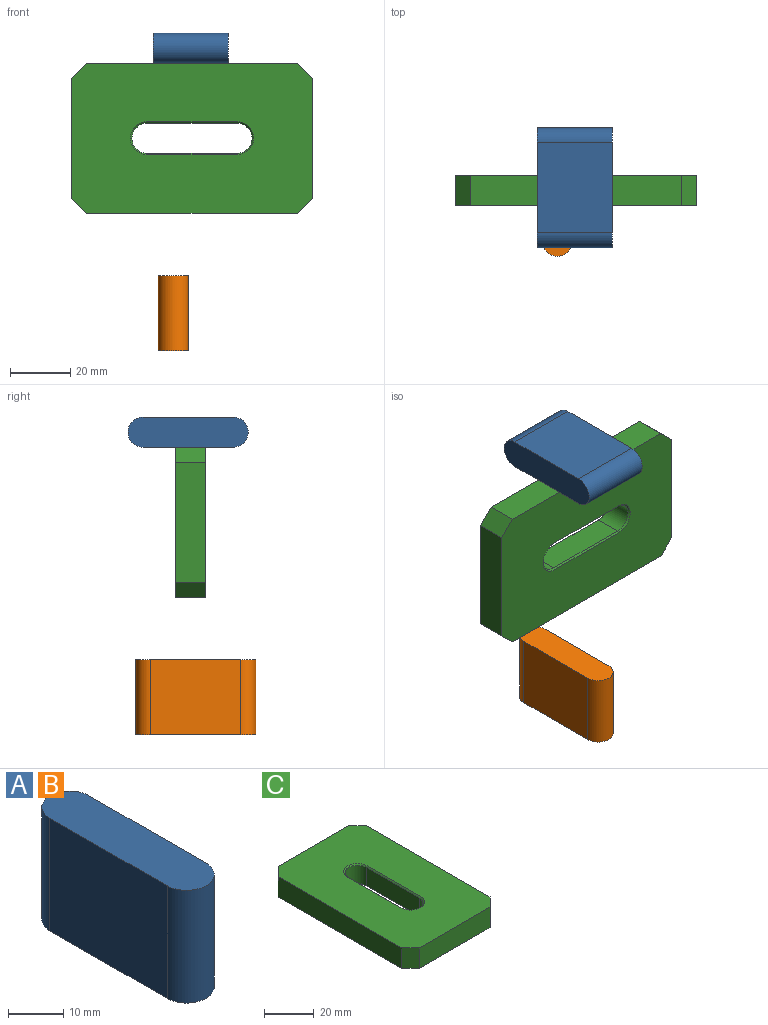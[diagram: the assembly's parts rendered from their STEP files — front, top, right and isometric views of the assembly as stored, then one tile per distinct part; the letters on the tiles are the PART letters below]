
ASSEMBLY  parts=3 mates=1
PART A: 6 faces, bbox 10x40x25 mm
  f0: cylinder r=5mm len=25mm, axis (0,0,1), area 392.7mm2, adj f1,f3,f4,f5
  f1: plane 30x25mm, normal (-1,0,0), area 750mm2, adj f0,f2,f4,f5
  f2: cylinder r=5mm len=25mm, axis (0,0,1), area 392.7mm2, adj f1,f3,f4,f5
  f3: plane 30x25mm, normal (1,0,0), area 750mm2, adj f0,f2,f4,f5
  f4: plane 40x10mm, normal (0,0,-1), area 378.5mm2, adj f0,f1,f2,f3
  f5: plane 40x10mm, normal (0,0,1), area 378.5mm2, adj f0,f1,f2,f3
PART B: same geometry as A
PART C: 22 faces, bbox 50x80x10 mm
  f0: plane 40x10mm, normal (0,1,0), area 400mm2, adj f8,f9,f10,f11
  f1: plane 70x10mm, normal (-1,0,0), area 700mm2, adj f8,f9,f11,f13
  f2: plane 40x10mm, normal (0,-1,0), area 400mm2, adj f8,f9,f12,f13
  f3: plane 30x9mm, normal (1,0,0), area 270mm2, adj f4,f6,f17,f19
  f4: cylinder r=5mm len=10mm, axis (0,0,-1), area 141.4mm2, adj f3,f5,f15,f18
  f5: plane 30x9mm, normal (-1,0,0), area 270mm2, adj f4,f6,f14,f20
  f6: cylinder r=5mm len=10mm, axis (0,0,-1), area 141.4mm2, adj f3,f5,f16,f21
  f7: plane 70x10mm, normal (1,0,0), area 700mm2, adj f8,f9,f10,f12
  f8: plane 80x50mm, normal (0,0,1), area 3525mm2, adj f0,f1,f2,f7,f10,f11,f12,f13
  f9: plane 80x50mm, normal (0,0,-1), area 3525mm2, adj f0,f1,f2,f7,f10,f11,f12,f13
  f10: plane 10x5mm, normal (0.71,0.71,0), area 70.7mm2, adj f0,f7,f8,f9
  f11: plane 10x5mm, normal (-0.71,0.71,0), area 70.7mm2, adj f0,f1,f8,f9
  f12: plane 10x5mm, normal (0.71,-0.71,0), area 70.7mm2, adj f2,f7,f8,f9
  f13: plane 10x5mm, normal (-0.71,-0.71,0), area 70.7mm2, adj f1,f2,f8,f9
  f14: plane 30x0.5mm, normal (-0.71,0,-0.71), area 21.2mm2, adj f5,f9,f15,f16
  f15: cone r=5.5mm half-angle=45deg, axis (0,0,-1), area 11.7mm2, adj f4,f9,f14,f17
  f16: cone r=5.5mm half-angle=45deg, axis (0,0,-1), area 11.7mm2, adj f6,f9,f14,f17
  f17: plane 30x0.5mm, normal (0.71,0,-0.71), area 21.2mm2, adj f3,f9,f15,f16
  f18: cone r=5mm half-angle=45deg, axis (0,0,1), area 11.7mm2, adj f4,f8,f19,f20
  f19: plane 30x0.5mm, normal (0.71,0,0.71), area 21.2mm2, adj f3,f8,f18,f21
  f20: plane 30x0.5mm, normal (-0.71,0,0.71), area 21.2mm2, adj f5,f8,f18,f21
  f21: cone r=5mm half-angle=45deg, axis (0,0,1), area 11.7mm2, adj f6,f8,f19,f20
PLACE A rot(axis=(0,1,0),90deg) t=(56.7,47.53,-40)mm
PLACE B t=(83.34,44.92,-70.81)mm
PLACE C rot(axis=(-0.58,-0.58,-0.58),120deg) t=(54.56,31.61,20)mm
MATE planar A.f3 <-> C.f7  axis (0,0,-1) through (44.2,37.53,0)mm
